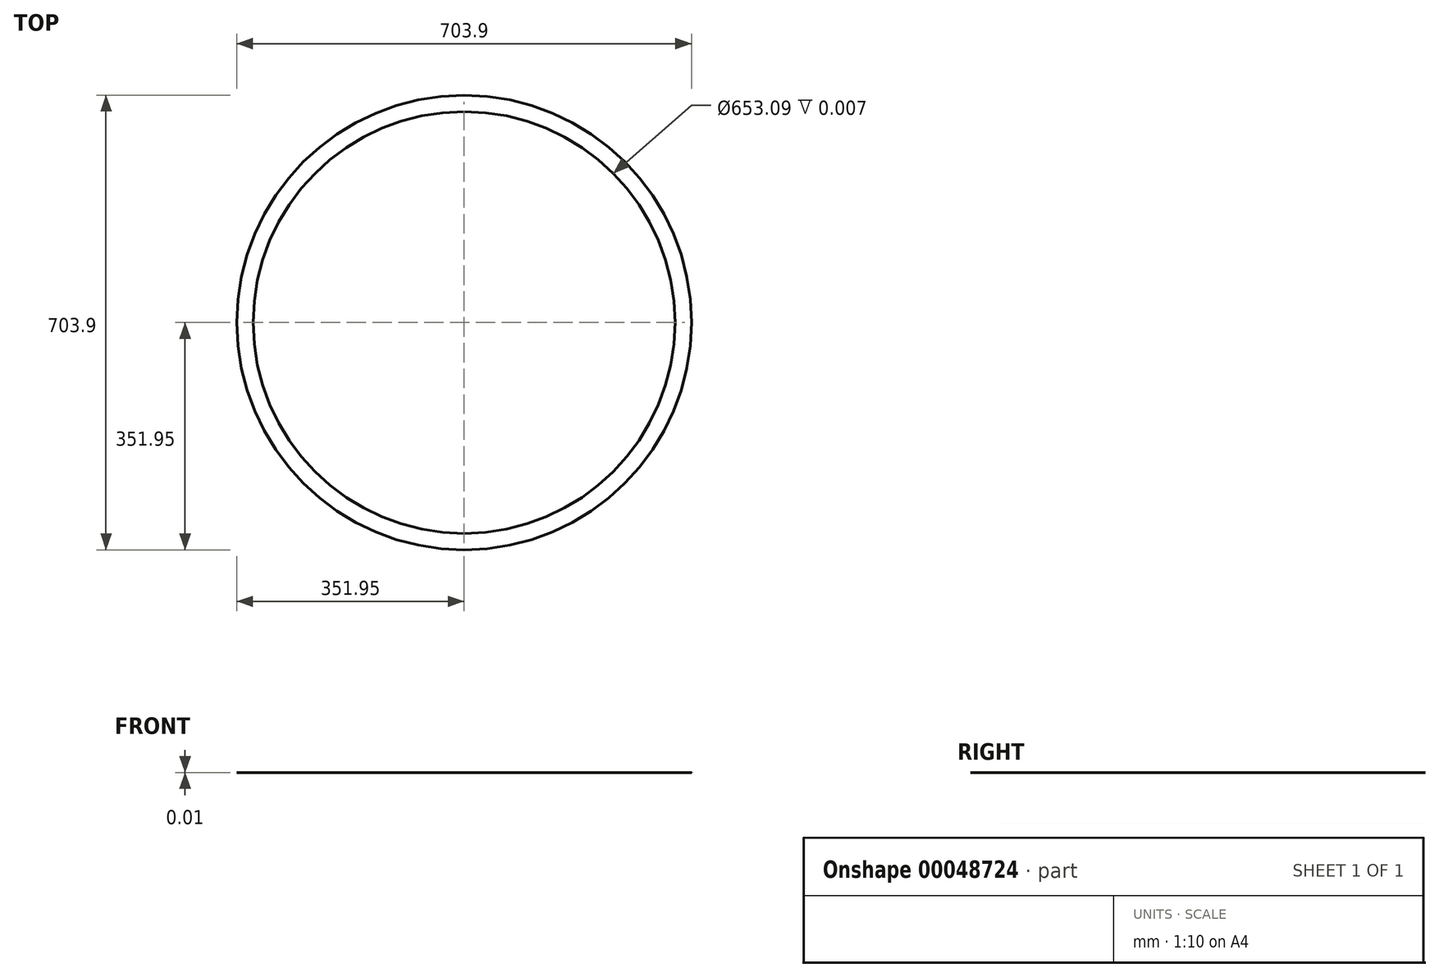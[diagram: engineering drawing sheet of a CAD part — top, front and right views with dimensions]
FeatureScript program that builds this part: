
annotation { "Feature Type Name" : "Feature", "Feature Type Description" : "" }
export const myFeature = defineFeature(function(context is Context, id is Id, definition is map)
    precondition{}
    {
        {
            var Q0;
            Q0=qCreatedBy(makeId("Top.planeOp"),FACE);
            var sketch = newSketch(context, id + "F0", { "sketchPlane" : qUnion([Q0])});
            skCircle(sketch, "E0", {"center": v(0, 0) * mm, "radius": 351.95 * mm});
            skCircle(sketch, "E1", {"center": v(0, 0) * mm, "radius": 326.55 * mm});
            skSolve(sketch);
        }
        {
            var Q0;
            Q0=makeQuery(id+"F0.imprint","IMPRINT",FACE,{"disambiguationData":[TD([[makeQuery(id+"F0.imprint","IMPRINT",EDGE,{"derivedFrom":sQuery(id+"F0.wireOp",EDGE,"E0")}),1.0]])]});
            extrude(context, id + "F1", {"entities" : qUnion([Q0]), "depth" : 3 / 406.4 * mm});
        }
    });
